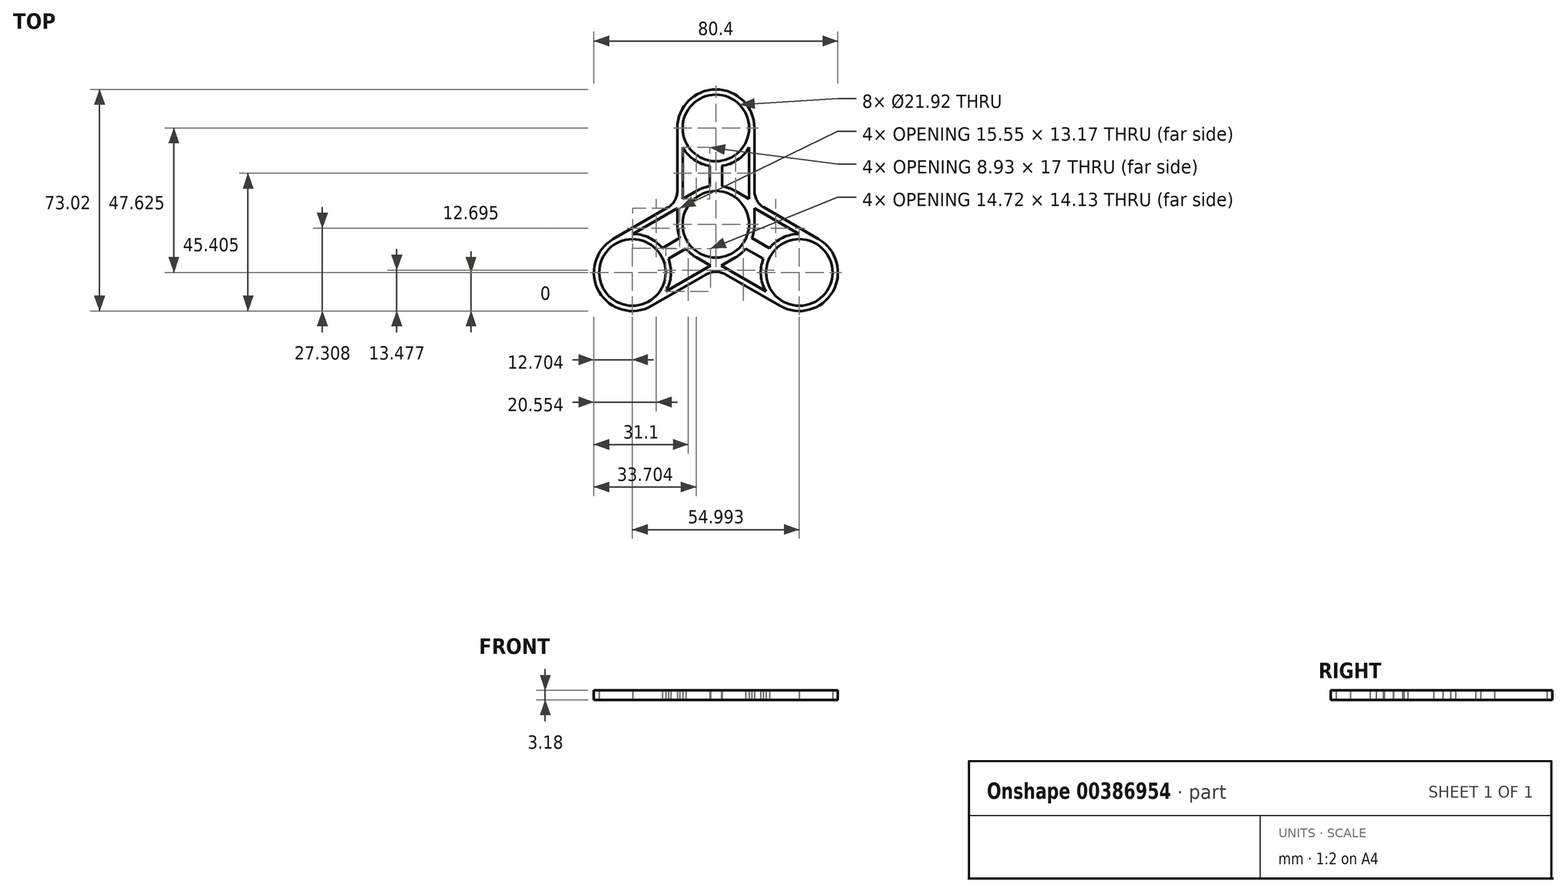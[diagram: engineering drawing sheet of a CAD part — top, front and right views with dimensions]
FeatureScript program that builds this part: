
annotation { "Feature Type Name" : "Feature", "Feature Type Description" : "" }
export const myFeature = defineFeature(function(context is Context, id is Id, definition is map)
    precondition{}
    {
        {
            var Q0;
            Q0=qCreatedBy(makeId("Top.planeOp"),FACE);
            var sketch = newSketch(context, id + "F0", { "sketchPlane" : qUnion([Q0])});
            skCircle(sketch, "E0", {"center": v(0, 0) * mm, "radius": 10.96 * mm});
            skCircle(sketch, "E1", {"center": v(0, 31.75) * mm, "radius": 10.96 * mm});
            skLineSegment(sketch, "E2", {"start": v(-10.96, 8.34) * mm, "end": v(-10.96, 25.33) * mm});
            skLineSegment(sketch, "E3", {"start": v(10.96, 25.33) * mm, "end": v(10.96, 8.34) * mm});
            skCircle(sketch, "E4", {"center": v(0, 31.75) * mm, "radius": 12.7 * mm});
            skCircle(sketch, "E5", {"center": v(0, 0) * mm, "radius": 12.7 * mm});
            skLineSegment(sketch, "E6", {"start": v(-12.7, 0) * mm, "end": v(-12.7, 5.32) * mm});
            skLineSegment(sketch, "E7", {"start": v(12.7, 31.75) * mm, "end": v(12.7, 11) * mm});
            skLineSegment(sketch, "E8", {"start": v(-2.03, 19.21) * mm, "end": v(-2.03, 12.54) * mm});
            skLineSegment(sketch, "E9", {"start": v(2.03, 19.21) * mm, "end": v(2.03, 12.54) * mm});
            skPoint(sketch, "E10.orphan", {"position": v(2.03, 31.75) * mm});
            skPoint(sketch, "E11.orphan", {"position": v(-2.03, 31.75) * mm});
            skPoint(sketch, "E12.orphan", {"position": v(-10.96, 31.75) * mm});
            skPoint(sketch, "E13.orphan", {"position": v(10.96, 31.75) * mm});
            skPoint(sketch, "E14.orphan", {"position": v(-10.96, 0) * mm});
            skPoint(sketch, "E15.orphan", {"position": v(10.96, 0) * mm});
            skLineSegment(sketch, "E16.1.0", {"start": v(-27.42, -3.18) * mm, "end": v(-12.7, 5.32) * mm});
            skLineSegment(sketch, "E16.1.1", {"start": v(-33.85, -4.88) * mm, "end": v(-15.87, 5.5) * mm});
            skLineSegment(sketch, "E16.1.2", {"start": v(-17.66, -7.85) * mm, "end": v(-11.87, -4.5) * mm});
            skLineSegment(sketch, "E16.1.3", {"start": v(-15.62, -11.37) * mm, "end": v(-9.84, -8.03) * mm});
            skLineSegment(sketch, "E16.1.4", {"start": v(6.35, -11) * mm, "end": v(1.74, -13.66) * mm});
            skLineSegment(sketch, "E16.1.5", {"start": v(-1.74, -13.66) * mm, "end": v(-16.46, -22.16) * mm});
            skCircle(sketch, "E16.1.6", {"center": v(-27.5, -15.87) * mm, "radius": 10.96 * mm});
            skCircle(sketch, "E16.1.7", {"center": v(-27.5, -15.87) * mm, "radius": 12.7 * mm});
            skLineSegment(sketch, "E16.2.0", {"start": v(16.46, -22.16) * mm, "end": v(1.74, -13.66) * mm});
            skLineSegment(sketch, "E16.2.1", {"start": v(21.15, -26.87) * mm, "end": v(3.17, -16.5) * mm});
            skLineSegment(sketch, "E16.2.2", {"start": v(15.62, -11.37) * mm, "end": v(9.84, -8.03) * mm});
            skLineSegment(sketch, "E16.2.3", {"start": v(17.66, -7.85) * mm, "end": v(11.87, -4.5) * mm});
            skLineSegment(sketch, "E16.2.4", {"start": v(6.35, 11) * mm, "end": v(10.96, 8.34) * mm});
            skLineSegment(sketch, "E16.2.5", {"start": v(12.7, 5.32) * mm, "end": v(27.42, -3.18) * mm});
            skCircle(sketch, "E16.2.6", {"center": v(27.5, -15.88) * mm, "radius": 10.96 * mm});
            skCircle(sketch, "E16.2.7", {"center": v(27.5, -15.88) * mm, "radius": 12.7 * mm});
            skPoint(sketch, "E17.orphan", {"position": v(-10.96, 6.42) * mm});
            skLineSegment(sketch, "E18.trimOffspring", {"start": v(-12.7, 11) * mm, "end": v(-12.7, 31.75) * mm});
            skLineSegment(sketch, "E19.trimOffspring", {"start": v(-10.96, 8.34) * mm, "end": v(-6.35, 11) * mm});
            skLineSegment(sketch, "E20.trimOffspring", {"start": v(12.7, 5.32) * mm, "end": v(12.7, 0) * mm});
            skLineSegment(sketch, "E21.trimOffspring", {"start": v(15.88, 5.5) * mm, "end": v(33.85, -4.88) * mm});
            skLineSegment(sketch, "E22.trimOffspring", {"start": v(-3.18, -16.5) * mm, "end": v(-21.15, -26.87) * mm});
            skLineSegment(sketch, "E23.trimOffspring", {"start": v(-1.74, -13.66) * mm, "end": v(-6.35, -11) * mm});
            skPoint(sketch, "E24.orphan", {"position": v(-0.08, -12.7) * mm});
            skPoint(sketch, "E25.orphan", {"position": v(0.08, -12.7) * mm});
            skPoint(sketch, "E26.orphan", {"position": v(10.96, 6.42) * mm});
            skPoint(sketch, "E27.orphan", {"position": v(11.04, 6.28) * mm});
            skPoint(sketch, "E28.orphan", {"position": v(-11.04, 6.28) * mm});
            skPoint(sketch, "E29.visualSharp", {"position": v(-12.7, 7.33) * mm});
            skArc(sketch, "E29.filletArc", {"start": v(-15.88, 5.5) * mm, "mid": v(-13.55, 7.82) * mm, "end": v(-12.7, 11) * mm});
            skPoint(sketch, "E30.visualSharp", {"position": v(12.7, 7.33) * mm});
            skArc(sketch, "E30.filletArc", {"start": v(12.7, 11) * mm, "mid": v(13.55, 7.82) * mm, "end": v(15.88, 5.5) * mm});
            skPoint(sketch, "E31.visualSharp", {"position": v(0, -14.66) * mm});
            skArc(sketch, "E31.filletArc", {"start": v(3.17, -16.5) * mm, "mid": v(0, -15.65) * mm, "end": v(-3.18, -16.5) * mm});
            skSolve(sketch);
        }
        {
            var Q0;
            {var subQ4=sQuery(id+"F0.wireOp",EDGE,"E2");Q0=makeQuery(id+"F0.imprint","IMPRINT",FACE,{"disambiguationData":[TD([[makeQuery(id+"F0.imprint","IMPRINT",EDGE,{"derivedFrom":subQ4}),1.0]])]});}
            var Q1;
            {var subQ4=sQuery(id+"F0.wireOp",EDGE,"E3");Q1=makeQuery(id+"F0.imprint","IMPRINT",FACE,{"disambiguationData":[TD([[makeQuery(id+"F0.imprint","IMPRINT",EDGE,{"derivedFrom":subQ4}),1.0]])]});}
            var Q2;
            Q2=makeQuery(id+"F0.imprint","IMPRINT",FACE,{"disambiguationData":[TD([[makeQuery(id+"F0.imprint","IMPRINT",EDGE,{"derivedFrom":sQuery(id+"F0.wireOp",EDGE,"E1")}),-1.0]])]});
            var Q3;
            {var subQ0=sQuery(id+"F0.wireOp",EDGE,"E8");Q3=makeQuery(id+"F0.imprint","IMPRINT",FACE,{"disambiguationData":[TD([[makeQuery(id+"F0.imprint","IMPRINT",EDGE,{"derivedFrom":subQ0}),1.0]])]});}
            var Q4;
            Q4=makeQuery(id+"F0.imprint","IMPRINT",FACE,{"disambiguationData":[TD([[makeQuery(id+"F0.imprint","IMPRINT",EDGE,{"derivedFrom":sQuery(id+"F0.wireOp",EDGE,"E0")}),-1.0]])]});
            var Q5;
            {var subQ0=sQuery(id+"F0.wireOp",EDGE,"E16.2.2");Q5=makeQuery(id+"F0.imprint","IMPRINT",FACE,{"disambiguationData":[TD([[makeQuery(id+"F0.imprint","IMPRINT",EDGE,{"derivedFrom":subQ0}),-1.0]])]});}
            var Q6;
            {var subQ3=sQuery(id+"F0.wireOp",EDGE,"E16.1.4");Q6=makeQuery(id+"F0.imprint","IMPRINT",FACE,{"disambiguationData":[TD([[makeQuery(id+"F0.imprint","IMPRINT",EDGE,{"derivedFrom":subQ3}),-1.0]])]});}
            var Q7;
            {var subQ0=sQuery(id+"F0.wireOp",EDGE,"E16.1.2");Q7=makeQuery(id+"F0.imprint","IMPRINT",FACE,{"disambiguationData":[TD([[makeQuery(id+"F0.imprint","IMPRINT",EDGE,{"derivedFrom":subQ0}),-1.0]])]});}
            var Q8;
            Q8=makeQuery(id+"F0.imprint","IMPRINT",FACE,{"disambiguationData":[TD([[makeQuery(id+"F0.imprint","IMPRINT",EDGE,{"derivedFrom":sQuery(id+"F0.wireOp",EDGE,"E16.1.6")}),-1.0]])]});
            var Q9;
            Q9=makeQuery(id+"F0.imprint","IMPRINT",FACE,{"disambiguationData":[TD([[makeQuery(id+"F0.imprint","IMPRINT",EDGE,{"derivedFrom":sQuery(id+"F0.wireOp",EDGE,"E16.2.6")}),-1.0]])]});
            extrude(context, id + "F1", {"entities" : qUnion([Q0, Q1, Q2, Q3, Q4, Q5, Q6, Q7, Q8, Q9]), "depth" : 3.17 * mm, "offsetDistance" : 25.4 * mm});
        }
    });
